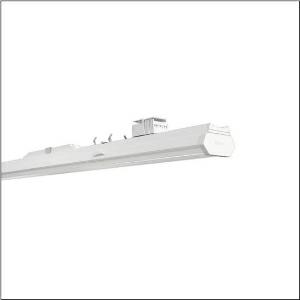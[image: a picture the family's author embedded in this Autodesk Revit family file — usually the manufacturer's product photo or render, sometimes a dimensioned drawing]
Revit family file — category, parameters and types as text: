
# Revit family: licross_r__11_protected_ho_51td1bdn6dxm_577c
name_source: partatom
category: Lighting Fixtures
units: mm (PartAtom-declared; Revit-internal decimal feet)

## family parameters
Cut with Voids When Loaded = No
Host = Face
Light Source = No
Part Type = Normal
Room Calculation Point = No
Round Connector Dimension = Use Diameter
Shared = No

## types (1)
- --- (1 x LED, 13290 lm, 81.3 W, 6500K)
    Apparent Load = 81 VA
    CIE Flux Codes = 54 82 95 97 100
    Color Rendering = 80
    Color Temperature = 6500K
    Default Elevation = 1800 mm
    Description = Licross® 11 Protected HO, luminaire insert, of sheet steel, galvanised, coil coated, white, length: 1.500mm, width: 90mm, height: 101mm, LED rated luminous flux: 13.290lm, light colour: 865, control gear: DALI 2, with plug, 5-pole, with phase selection, mains connection: 220..240V, AC, 50/60Hz, rated input power: 81W, internal wiring halogen-free, primary optical cover: cover, of PMMA, light emission: direct distribution, primary light characteristic: symmetric, protection rating (complete): IP54, insulation class (complete): insulation class I (protective earthing), certification: CE, ENEC, VDE, UKCA, protection symbol: D if used in an environment with non-conductive dust loads with corresponding accessories, impact resistance: IK06, permissible ambient temperature for indoor applications: -25..+35°C, corresponds to IFS (International Featured Standards) requirements for safety and quality in the food industry, reducing of maximum allowable ambient temperature of 5°C with ceiling mounting, LABS conformity tested according to VDMA 24364:2018-05, packaging unit: 1 piece
    Height = 92 mm
    Lamp = 1 x LED
    Lamp Light Flux = 13290 lm
    Lamp Power = 81.3 W
    Lamp count = 1
    Length = 1500 mm
    Luminous efficacy = 163 lm/W
    Manufacturer = Siteco
    ModVariant = No
    Model = 51TD1BDN6DXM
    Mounting Place = Ceiling
    Mounting Type = Pendant
    Number of Poles = 1
    OnlyDefault = Yes
    Power Factor = 1
    Product Name = Licross® 11 Protected HO
    Product group = luminaire insert | ceiling pendant
    ProductGroupID = 902
    Protection Class = Protection class I
    Protection Degree = IP 54
    RLX_Detail_Level = 1
    RLX_Emergency_Light_Flux = 0 lm
    RLX_Emergency_Type = 0
    RLX_Emergency_Type_DB = No
    RlxData = <blob elided: 24413 chars, md5=00019002>
    Socket = socket
    Standby Power = 0 W
    System Light Flux = 13290 lm
    System Power = 81 W
    Type Comments = factory setting: luminous flux: 100 % | dim-lin: 254 | 550 mA
    Type Image = l_1256145.jpg
    URL = http://relux.com
    VarID = @adj_030151
    Voltage = 0 V
    Weight = 0.00 kg
    Width = 88 mm

## geometry (parser evidence)
native form markers: Blend x4, Sweep x9
no freeform markers — native parametric forms only
